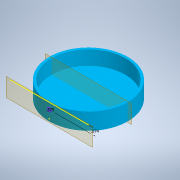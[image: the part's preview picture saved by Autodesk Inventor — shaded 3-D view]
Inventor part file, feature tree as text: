
AUTODESK INVENTOR PART (.ipt)
format: ipt  version: 2021 (Build 250183000, 183)  size: 128,000 bytes
history: native  units: in
note: dims shown in document units (in); Inventor stores cm internally (conversion verified against a paired STEP export)
features: extrude x3, sketch x3, plane x1
ambient origin geometry x8: Origin, YZ Plane, XZ Plane, XY Plane, X Axis, Y Axis, Z Axis, Center Point
bodies: Solid1 (feature_tree)
feature tree (7):
  extrude  "Extrusion1"  Depth=0.25in TaperAngle=0.0deg
  extrude  "Extrusion2"  Depth=1.5in TaperAngle=0.0deg
  plane  "Work Plane1"
  extrude  "Extrusion3"  Depth=0.674in
  sketch  "Sketch1"  dims[d0=8.25in d1=0.25in d2=0.0in]
  sketch  "Sketch2"  dims[d3=0.25in d4=1.5in d5=0.0in]
  sketch  "Sketch3"  dims[d6=0.375in d7=0.674in d8=0.0in d9=0.0in]
